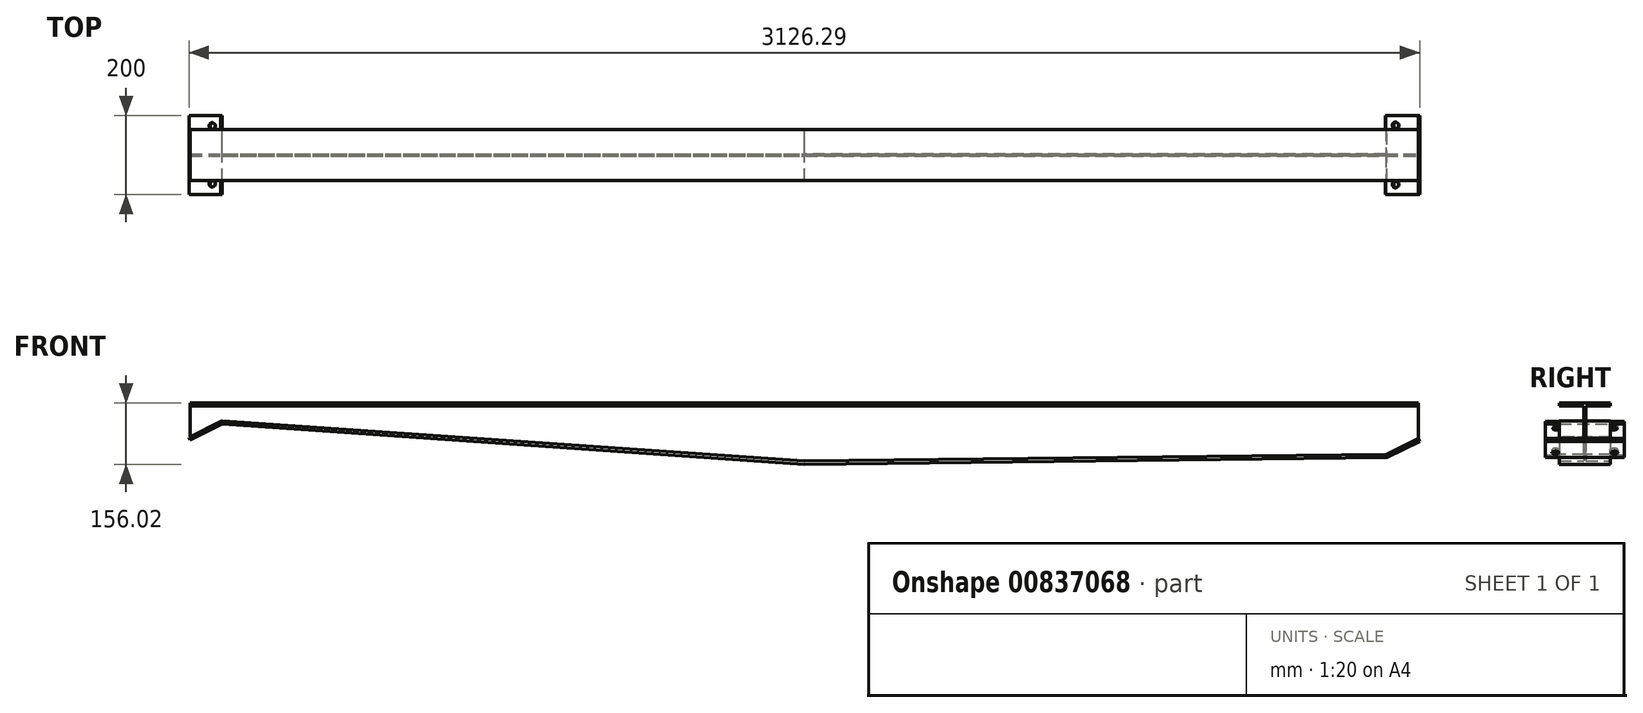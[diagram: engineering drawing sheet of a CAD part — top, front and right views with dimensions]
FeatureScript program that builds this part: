
annotation { "Feature Type Name" : "Feature", "Feature Type Description" : "" }
export const myFeature = defineFeature(function(context is Context, id is Id, definition is map)
    precondition{}
    {
        {
            var Q0;
            Q0=qCreatedBy(makeId("Front.planeOp"),FACE);
            var sketch = newSketch(context, id + "F0", { "sketchPlane" : qUnion([Q0])});
            skLineSegment(sketch, "E0", {"start": v(0, 140) * mm, "end": v(-1560, 140) * mm});
            skLineSegment(sketch, "E1.MirrorCS", {"start": v(0, 140) * mm, "end": v(1560, 140) * mm});
            skLineSegment(sketch, "E2", {"start": v(1560, 140) * mm, "end": v(1560, 56.88) * mm});
            skLineSegment(sketch, "E3", {"start": v(1560, 56.88) * mm, "end": v(1479.32, 17) * mm});
            skLineSegment(sketch, "E4", {"start": v(1479.32, 17) * mm, "end": v(0, 0) * mm});
            skLineSegment(sketch, "E5", {"start": v(-1560, 62.12) * mm, "end": v(-1479.32, 102) * mm});
            skLineSegment(sketch, "E6", {"start": v(-1560, 62.12) * mm, "end": v(-1560, 140) * mm});
            skLineSegment(sketch, "E7", {"start": v(-1479.32, 102) * mm, "end": v(0, 0) * mm});
            skSolve(sketch);
        }
        {
            var Q0;
            Q0=qSketchRegion(id+"F0",true);
            extrude(context, id + "F1", {"entities" : qUnion([Q0]), "depth" : 5 * mm, "offsetDistance" : 25 * mm, "symmetric" : true});
        }
        {
            var Q0;
            Q0=qCreatedBy(makeId("Front.planeOp"),FACE);
            var sketch = newSketch(context, id + "F2", { "sketchPlane" : qUnion([Q0])});
            skLineSegment(sketch, "E8", {"start": v(0, 0) * mm, "end": v(-1479.32, 102) * mm});
            skLineSegment(sketch, "E9", {"start": v(-1479.32, 93.98) * mm, "end": v(0, -8.02) * mm});
            skLineSegment(sketch, "E10", {"start": v(0, 140) * mm, "end": v(-1560, 140) * mm});
            skLineSegment(sketch, "E11", {"start": v(-1560, 140) * mm, "end": v(-1560, 148) * mm});
            skLineSegment(sketch, "E12", {"start": v(-1560, 148) * mm, "end": v(0, 148) * mm});
            skLineSegment(sketch, "E13.MirrorCS", {"start": v(0, 140) * mm, "end": v(1560, 140) * mm});
            skLineSegment(sketch, "E14.MirrorCS", {"start": v(1560, 148) * mm, "end": v(0, 148) * mm});
            skLineSegment(sketch, "E15.MirrorCS", {"start": v(1560, 140) * mm, "end": v(1560, 148) * mm});
            skLineSegment(sketch, "E16", {"start": v(1560, 56.88) * mm, "end": v(1479.32, 17) * mm});
            skLineSegment(sketch, "E17", {"start": v(1479.32, 17) * mm, "end": v(0, 0) * mm});
            skLineSegment(sketch, "E18", {"start": v(1560, 56.88) * mm, "end": v(1560, 48.86) * mm});
            skLineSegment(sketch, "E19", {"start": v(1560, 48.86) * mm, "end": v(1479.32, 8.98) * mm});
            skLineSegment(sketch, "E20", {"start": v(1479.32, 8.98) * mm, "end": v(0, -8.02) * mm});
            skLineSegment(sketch, "E21", {"start": v(-1479.32, 102) * mm, "end": v(-1560, 62.12) * mm});
            skLineSegment(sketch, "E22", {"start": v(-1560, 62.12) * mm, "end": v(-1560, 54.1) * mm});
            skLineSegment(sketch, "E23", {"start": v(-1560, 54.1) * mm, "end": v(-1479.32, 93.98) * mm});
            skSolve(sketch);
        }
        {
            var Q0;
            Q0=qSketchRegion(id+"F2",true);
            extrude(context, id + "F3", {"entities" : qUnion([Q0]), "operationType" : NewBodyOperationType.ADD, "depth" : 130 * mm, "offsetDistance" : 25 * mm, "symmetric" : true});
        }
        {
            var Q0;
            Q0=qCreatedBy(makeId("Front.planeOp"),FACE);
            var sketch = newSketch(context, id + "F4", { "sketchPlane" : qUnion([Q0])});
            skLineSegment(sketch, "E24", {"start": v(0, 0) * mm, "end": v(0, -96.56) * mm, "construction": true});
            skLineSegment(sketch, "E25", {"start": v(0, -96.56) * mm, "end": v(-31.38, 0) * mm, "construction": true});
            skSolve(sketch);
        }
        {
            var Q0;
            Q0=makeQuery(id+"F3.opExtrude","SWEPT_FACE",FACE,{"disambiguationData":[OSD([sQuery(id+"F2.wireOp",EDGE,"E19")])]});
            var sketch = newSketch(context, id + "F5", { "sketchPlane" : qUnion([Q0])});
            skLineSegment(sketch, "E26.bottom", {"start": v(1423.72, 100) * mm, "end": v(1330.17, 100) * mm});
            skLineSegment(sketch, "E26.top", {"start": v(1423.72, -100) * mm, "end": v(1330.17, -100) * mm});
            skLineSegment(sketch, "E26.left", {"start": v(1423.72, 100) * mm, "end": v(1423.72, -100) * mm});
            skLineSegment(sketch, "E26.right", {"start": v(1330.17, 100) * mm, "end": v(1330.17, -100) * mm});
            skLineSegment(sketch, "E27", {"start": v(1423.72, 0) * mm, "end": v(1330.17, 0) * mm, "construction": true});
            skCircle(sketch, "E28", {"center": v(1358.72, 75) * mm, "radius": 8.5 * mm});
            skCircle(sketch, "E29.MirrorC", {"center": v(1358.72, -75) * mm, "radius": 8.5 * mm});
            skSolve(sketch);
        }
        {
            var Q0;
            Q0=qSketchRegion(id+"F5",true);
            extrude(context, id + "F6", {"entities" : qUnion([Q0]), "operationType" : NewBodyOperationType.ADD, "oppositeDirection" : true, "depth" : 8 * mm, "offsetDistance" : 25 * mm});
        }
        {
            var Q0;
            Q0=makeQuery(id+"F3.opExtrude","SWEPT_FACE",FACE,{"disambiguationData":[OSD([sQuery(id+"F2.wireOp",EDGE,"E23")])]});
            var sketch = newSketch(context, id + "F7", { "sketchPlane" : qUnion([Q0])});
            skLineSegment(sketch, "E30.bottom", {"start": v(-1374.55, 100) * mm, "end": v(-1284.55, 100) * mm});
            skLineSegment(sketch, "E30.top", {"start": v(-1374.55, -100) * mm, "end": v(-1284.55, -100) * mm});
            skLineSegment(sketch, "E30.left", {"start": v(-1374.55, 100) * mm, "end": v(-1374.55, -100) * mm});
            skLineSegment(sketch, "E30.right", {"start": v(-1284.55, 100) * mm, "end": v(-1284.55, -100) * mm});
            skLineSegment(sketch, "E31", {"start": v(-1374.55, 0) * mm, "end": v(-1284.55, 0) * mm, "construction": true});
            skCircle(sketch, "E32", {"center": v(-1309.55, -73.4) * mm, "radius": 8.5 * mm});
            skCircle(sketch, "E33.MirrorC", {"center": v(-1309.55, 73.4) * mm, "radius": 8.5 * mm});
            skSolve(sketch);
        }
        {
            var Q0;
            Q0=qSketchRegion(id+"F7",true);
            extrude(context, id + "F8", {"entities" : qUnion([Q0]), "operationType" : NewBodyOperationType.ADD, "oppositeDirection" : true, "depth" : 7 * mm, "offsetDistance" : 25 * mm});
        }
    });
